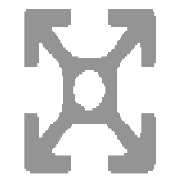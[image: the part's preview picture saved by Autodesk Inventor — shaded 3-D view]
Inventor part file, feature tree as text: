
AUTODESK INVENTOR PART (.ipt)
format: ipt  version: 2023 (Build 270158000, 158)  size: 239,616 bytes
history: native  units: mm
features: other x4, plane x3, sketch x3, split x2
ambient origin geometry x8: Origin, YZ Plane, XZ Plane, XY Plane, X Axis, Y Axis, Z Axis, Center Point
bodies: Solid1 (feature_tree), Body (feature_tree)
feature tree (12):
  other  "Driven Length"
  other  "Frame Generator"
  other  "Start Plane"
  other  "End Plane"
  plane  "Work Plane5"
  split  "Split1"
  plane  "Work Plane6"
  split  "Split2"
  sketch  "Sketch"  dims[d5=7.0mm d6=2.0mm d7=0.5mm d8=1.0mm d9=20.0mm d10=20.0mm d11=8.0mm d13=5.0mm d14=8.0mm d17=-10.0mm d18=670.4mm d19=0.13mm d20=0.0mm d23=90.0deg d22=680.4mm]
  sketch  "Sketch4"  dims[d3=2.0mm]
  plane  "Work Plane4"
  sketch  "Sketch5"  dims[d4=2.0mm]
